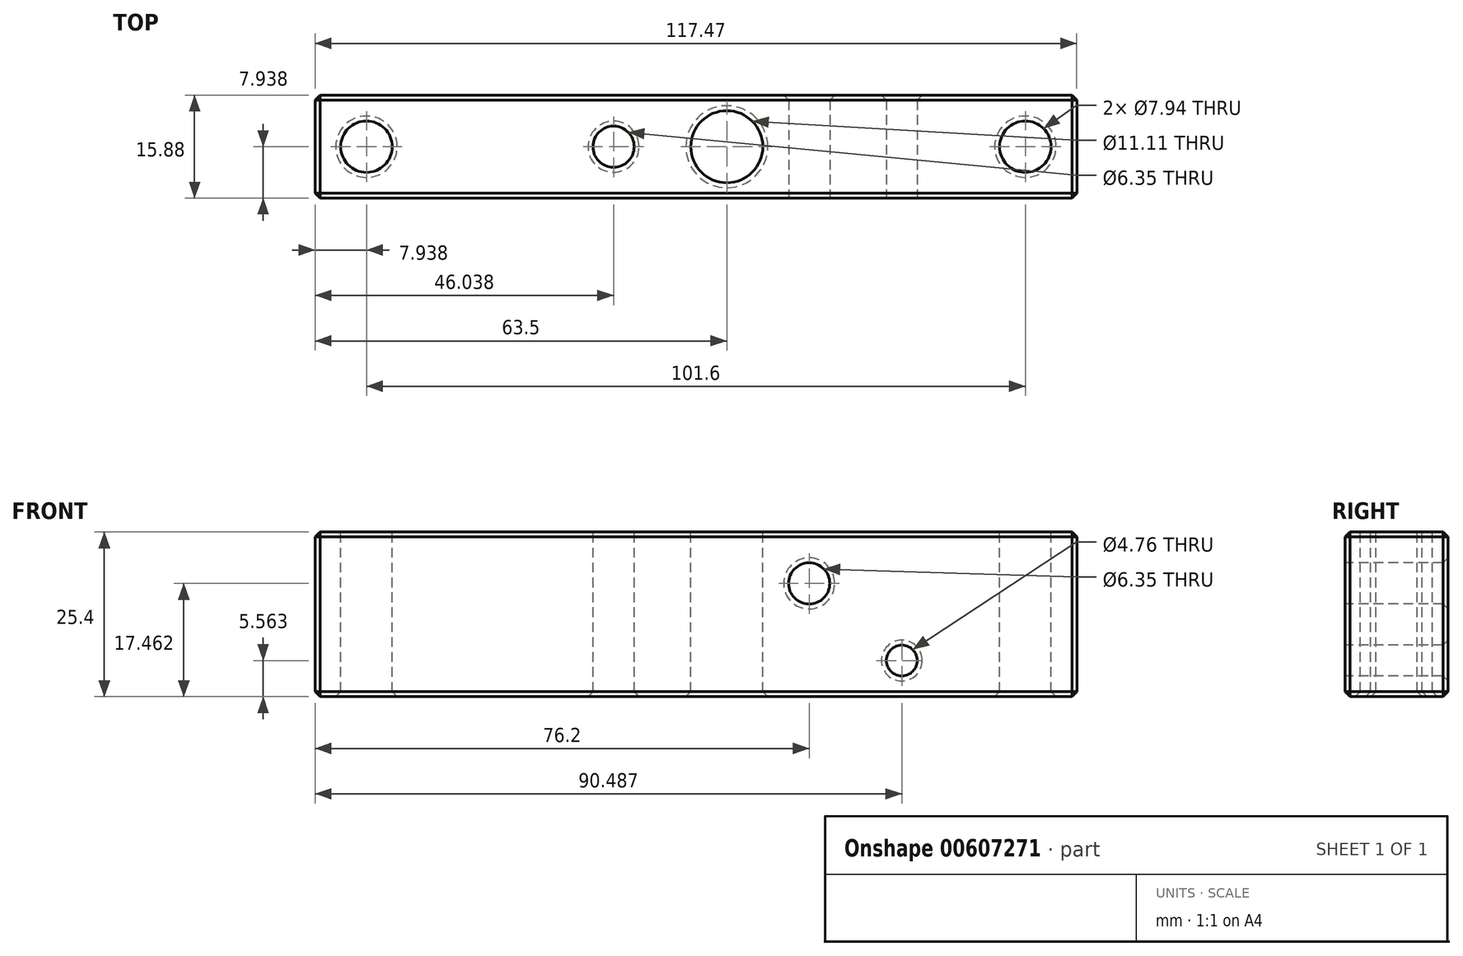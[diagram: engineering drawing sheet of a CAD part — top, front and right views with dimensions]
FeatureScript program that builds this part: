
annotation { "Feature Type Name" : "Feature", "Feature Type Description" : "" }
export const myFeature = defineFeature(function(context is Context, id is Id, definition is map)
    precondition{}
    {
        {
            var Q0;
            Q0=qCreatedBy(makeId("Top.planeOp"),FACE);
            var sketch = newSketch(context, id + "F0", { "sketchPlane" : qUnion([Q0])});
            skLineSegment(sketch, "E0.bottom", {"start": v(0, 0) * mm, "end": v(117.48, 0) * mm});
            skLineSegment(sketch, "E0.top", {"start": v(0, 15.88) * mm, "end": v(117.48, 15.88) * mm});
            skLineSegment(sketch, "E0.left", {"start": v(0, 0) * mm, "end": v(0, 15.88) * mm});
            skLineSegment(sketch, "E0.right", {"start": v(117.48, 0) * mm, "end": v(117.48, 15.88) * mm});
            skSolve(sketch);
        }
        {
            var Q0;
            Q0 = qSketchRegion(id + "F0", true);
            extrude(context, id + "F1", {"entities" : qUnion([Q0]), "depth" : 25.4 * mm, "offsetDistance" : 25.4 * mm});
        }
        {
            var Q0;
            Q0=makeQuery(id+"F1.opExtrude","CAP_FACE",FACE,{"disambiguationData":[OSD([sQuery(id+"F0.wireOp",EDGE,"E0.bottom"),sQuery(id+"F0.wireOp",EDGE,"E0.top"),sQuery(id+"F0.wireOp",EDGE,"E0.left"),sQuery(id+"F0.wireOp",EDGE,"E0.right")])],"isStart":false});
            var sketch = newSketch(context, id + "F2", { "sketchPlane" : qUnion([Q0])});
            skPoint(sketch, "E1.endSnap0", {"position": v(117.48, 7.94) * mm});
            skCircle(sketch, "E2", {"center": v(109.54, 7.94) * mm, "radius": 3.97 * mm});
            skCircle(sketch, "E3", {"center": v(7.94, 7.94) * mm, "radius": 3.97 * mm});
            skLineSegment(sketch, "E4", {"start": v(117.48, 7.94) * mm, "end": v(109.54, 7.94) * mm, "construction": true});
            skLineSegment(sketch, "E5", {"start": v(0, 7.94) * mm, "end": v(7.94, 7.94) * mm, "construction": true});
            skLineSegment(sketch, "E6", {"start": v(117.48, 7.94) * mm, "end": v(63.5, 7.94) * mm, "construction": true});
            skLineSegment(sketch, "E7", {"start": v(117.48, 7.94) * mm, "end": v(46.04, 7.94) * mm, "construction": true});
            skCircle(sketch, "E8", {"center": v(63.5, 7.94) * mm, "radius": 5.56 * mm});
            skCircle(sketch, "E9", {"center": v(46.04, 7.94) * mm, "radius": 3.18 * mm});
            skSolve(sketch);
        }
        {
            var Q0;
            Q0=makeQuery(id+"F2.imprint","IMPRINT",FACE,{"disambiguationData":[TD([[makeQuery(id+"F2.imprint","IMPRINT",EDGE,{"derivedFrom":sQuery(id+"F2.wireOp",EDGE,"E3")}),1.0]])]});
            var Q1;
            Q1=makeQuery(id+"F2.imprint","IMPRINT",FACE,{"disambiguationData":[TD([[makeQuery(id+"F2.imprint","IMPRINT",EDGE,{"derivedFrom":sQuery(id+"F2.wireOp",EDGE,"E9")}),1.0]])]});
            var Q2;
            Q2=makeQuery(id+"F2.imprint","IMPRINT",FACE,{"disambiguationData":[TD([[makeQuery(id+"F2.imprint","IMPRINT",EDGE,{"derivedFrom":sQuery(id+"F2.wireOp",EDGE,"E8")}),1.0]])]});
            var Q3;
            Q3=makeQuery(id+"F2.imprint","IMPRINT",FACE,{"disambiguationData":[TD([[makeQuery(id+"F2.imprint","IMPRINT",EDGE,{"derivedFrom":sQuery(id+"F2.wireOp",EDGE,"E2")}),1.0]])]});
            extrude(context, id + "F3", {"entities" : qUnion([Q0, Q1, Q2, Q3]), "operationType" : NewBodyOperationType.REMOVE, "endBound" : BoundingType.THROUGH_ALL, "oppositeDirection" : true, "depth" : 25.4 * mm, "offsetDistance" : 25.4 * mm});
        }
        {
            var Q0;
            Q0=makeQuery(id+"F1.opExtrude","SWEPT_FACE",FACE,{"disambiguationData":[OSD([sQuery(id+"F0.wireOp",EDGE,"E0.bottom")])]});
            var sketch = newSketch(context, id + "F4", { "sketchPlane" : qUnion([Q0])});
            skLineSegment(sketch, "E10", {"start": v(117.48, 0) * mm, "end": v(117.48, 5.56) * mm, "construction": true});
            skLineSegment(sketch, "E11", {"start": v(117.48, 5.56) * mm, "end": v(90.49, 5.56) * mm, "construction": true});
            skLineSegment(sketch, "E12", {"start": v(117.48, 0) * mm, "end": v(117.48, 17.46) * mm, "construction": true});
            skLineSegment(sketch, "E13", {"start": v(117.48, 17.46) * mm, "end": v(76.2, 17.46) * mm, "construction": true});
            skCircle(sketch, "E14", {"center": v(76.2, 17.46) * mm, "radius": 3.18 * mm});
            skCircle(sketch, "E15", {"center": v(90.49, 5.56) * mm, "radius": 2.38 * mm});
            skSolve(sketch);
        }
        {
            var Q0;
            Q0 = qSketchRegion(id + "F4", true);
            extrude(context, id + "F5", {"entities" : qUnion([Q0]), "operationType" : NewBodyOperationType.REMOVE, "endBound" : BoundingType.THROUGH_ALL, "oppositeDirection" : true, "depth" : 25.4 * mm, "offsetDistance" : 25.4 * mm});
        }
        {
            var Q0;
            Q0=makeQuery(id+"F5.boolean.opBoolean","COPY",EDGE,{"derivedFrom":makeQuery(id+"F5.opExtrude","CAP_EDGE",EDGE,{"disambiguationData":[OSD([sQuery(id+"F4.wireOp",EDGE,"E14")])],"isStart":true})});
            var Q1;
            Q1=makeQuery(id+"F5.boolean.opBoolean","COPY",EDGE,{"derivedFrom":makeQuery(id+"F5.opExtrude","CAP_EDGE",EDGE,{"disambiguationData":[OSD([sQuery(id+"F4.wireOp",EDGE,"E15")])],"isStart":true})});
            var Q2;
            Q2=makeQuery(id+"F3.boolean.opBoolean","COPY",EDGE,{"derivedFrom":makeQuery(id+"F3.opExtrude","CAP_EDGE",EDGE,{"disambiguationData":[OSD([sQuery(id+"F2.wireOp",EDGE,"E8")])],"isStart":true})});
            var Q3;
            Q3=makeQuery(id+"F3.boolean.opBoolean","COPY",EDGE,{"derivedFrom":makeQuery(id+"F3.opExtrude","CAP_EDGE",EDGE,{"disambiguationData":[OSD([sQuery(id+"F2.wireOp",EDGE,"E9")])],"isStart":true})});
            var Q4;
            Q4=makeQuery(id+"F3.boolean.opBoolean","COPY",EDGE,{"derivedFrom":makeQuery(id+"F3.opExtrude","CAP_EDGE",EDGE,{"disambiguationData":[OSD([sQuery(id+"F2.wireOp",EDGE,"E2")])],"isStart":true})});
            var Q5;
            Q5=makeQuery(id+"F1.opExtrude","CAP_EDGE",EDGE,{"disambiguationData":[OSD([sQuery(id+"F0.wireOp",EDGE,"E0.bottom")])],"isStart":false});
            var Q6;
            Q6=makeQuery(id+"F1.opExtrude","CAP_EDGE",EDGE,{"disambiguationData":[OSD([sQuery(id+"F0.wireOp",EDGE,"E0.bottom")])],"isStart":true});
            var Q7;
            Q7=makeQuery(id+"F1.opExtrude","SWEPT_EDGE",EDGE,{"disambiguationData":[OSD([sQuery(id+"F0.wireOp",EDGE,"E0.bottom"),sQuery(id+"F0.wireOp",EDGE,"E0.right")])]});
            var Q8;
            Q8=makeQuery(id+"F1.opExtrude","SWEPT_EDGE",EDGE,{"disambiguationData":[OSD([sQuery(id+"F0.wireOp",EDGE,"E0.bottom"),sQuery(id+"F0.wireOp",EDGE,"E0.left")])]});
            var Q9;
            Q9=makeQuery(id+"F1.opExtrude","CAP_EDGE",EDGE,{"disambiguationData":[OSD([sQuery(id+"F0.wireOp",EDGE,"E0.left")])],"isStart":false});
            var Q10;
            Q10=makeQuery(id+"F1.opExtrude","SWEPT_EDGE",EDGE,{"disambiguationData":[OSD([sQuery(id+"F0.wireOp",EDGE,"E0.top"),sQuery(id+"F0.wireOp",EDGE,"E0.left")])]});
            var Q11;
            Q11=makeQuery(id+"F1.opExtrude","CAP_EDGE",EDGE,{"disambiguationData":[OSD([sQuery(id+"F0.wireOp",EDGE,"E0.left")])],"isStart":true});
            var Q12;
            Q12=makeQuery(id+"F1.opExtrude","CAP_EDGE",EDGE,{"disambiguationData":[OSD([sQuery(id+"F0.wireOp",EDGE,"E0.top")])],"isStart":true});
            var Q13;
            Q13=makeQuery(id+"F3.boolean.opBoolean","INTERSECT",EDGE,{"derivedFrom":[makeQuery(id+"F1.opExtrude","CAP_FACE",FACE,{"disambiguationData":[OSD([sQuery(id+"F0.wireOp",EDGE,"E0.bottom"),sQuery(id+"F0.wireOp",EDGE,"E0.top"),sQuery(id+"F0.wireOp",EDGE,"E0.left"),sQuery(id+"F0.wireOp",EDGE,"E0.right")])],"isStart":true}),makeQuery(id+"F3.opExtrude","SWEPT_FACE",FACE,{"disambiguationData":[OSD([sQuery(id+"F2.wireOp",EDGE,"E3")])]})]});
            var Q14;
            Q14=makeQuery(id+"F3.boolean.opBoolean","INTERSECT",EDGE,{"derivedFrom":[makeQuery(id+"F1.opExtrude","CAP_FACE",FACE,{"disambiguationData":[OSD([sQuery(id+"F0.wireOp",EDGE,"E0.bottom"),sQuery(id+"F0.wireOp",EDGE,"E0.top"),sQuery(id+"F0.wireOp",EDGE,"E0.left"),sQuery(id+"F0.wireOp",EDGE,"E0.right")])],"isStart":true}),makeQuery(id+"F3.opExtrude","SWEPT_FACE",FACE,{"disambiguationData":[OSD([sQuery(id+"F2.wireOp",EDGE,"E9")])]})]});
            var Q15;
            Q15=makeQuery(id+"F3.boolean.opBoolean","INTERSECT",EDGE,{"derivedFrom":[makeQuery(id+"F1.opExtrude","CAP_FACE",FACE,{"disambiguationData":[OSD([sQuery(id+"F0.wireOp",EDGE,"E0.bottom"),sQuery(id+"F0.wireOp",EDGE,"E0.top"),sQuery(id+"F0.wireOp",EDGE,"E0.left"),sQuery(id+"F0.wireOp",EDGE,"E0.right")])],"isStart":true}),makeQuery(id+"F3.opExtrude","SWEPT_FACE",FACE,{"disambiguationData":[OSD([sQuery(id+"F2.wireOp",EDGE,"E8")])]})]});
            var Q16;
            Q16=makeQuery(id+"F1.opExtrude","CAP_EDGE",EDGE,{"disambiguationData":[OSD([sQuery(id+"F0.wireOp",EDGE,"E0.top")])],"isStart":false});
            var Q17;
            Q17=makeQuery(id+"F5.boolean.opBoolean","INTERSECT",EDGE,{"derivedFrom":[makeQuery(id+"F1.opExtrude","SWEPT_FACE",FACE,{"disambiguationData":[OSD([sQuery(id+"F0.wireOp",EDGE,"E0.top")])]}),makeQuery(id+"F5.opExtrude","SWEPT_FACE",FACE,{"disambiguationData":[OSD([sQuery(id+"F4.wireOp",EDGE,"E14")])]})]});
            var Q18;
            Q18=makeQuery(id+"F5.boolean.opBoolean","INTERSECT",EDGE,{"derivedFrom":[makeQuery(id+"F1.opExtrude","SWEPT_FACE",FACE,{"disambiguationData":[OSD([sQuery(id+"F0.wireOp",EDGE,"E0.top")])]}),makeQuery(id+"F5.opExtrude","SWEPT_FACE",FACE,{"disambiguationData":[OSD([sQuery(id+"F4.wireOp",EDGE,"E15")])]})]});
            var Q19;
            Q19=makeQuery(id+"F3.boolean.opBoolean","COPY",EDGE,{"derivedFrom":makeQuery(id+"F3.opExtrude","CAP_EDGE",EDGE,{"disambiguationData":[OSD([sQuery(id+"F2.wireOp",EDGE,"E3")])],"isStart":true})});
            var Q20;
            Q20=makeQuery(id+"F1.opExtrude","CAP_EDGE",EDGE,{"disambiguationData":[OSD([sQuery(id+"F0.wireOp",EDGE,"E0.right")])],"isStart":false});
            var Q21;
            Q21=makeQuery(id+"F1.opExtrude","SWEPT_EDGE",EDGE,{"disambiguationData":[OSD([sQuery(id+"F0.wireOp",EDGE,"E0.top"),sQuery(id+"F0.wireOp",EDGE,"E0.right")])]});
            var Q22;
            Q22=makeQuery(id+"F1.opExtrude","CAP_EDGE",EDGE,{"disambiguationData":[OSD([sQuery(id+"F0.wireOp",EDGE,"E0.right")])],"isStart":true});
            var Q23;
            Q23=makeQuery(id+"F3.boolean.opBoolean","INTERSECT",EDGE,{"derivedFrom":[makeQuery(id+"F1.opExtrude","CAP_FACE",FACE,{"disambiguationData":[OSD([sQuery(id+"F0.wireOp",EDGE,"E0.bottom"),sQuery(id+"F0.wireOp",EDGE,"E0.top"),sQuery(id+"F0.wireOp",EDGE,"E0.left"),sQuery(id+"F0.wireOp",EDGE,"E0.right")])],"isStart":true}),makeQuery(id+"F3.opExtrude","SWEPT_FACE",FACE,{"disambiguationData":[OSD([sQuery(id+"F2.wireOp",EDGE,"E2")])]})]});
            chamfer(context, id + "F6", {"entities" : qUnion([Q0, Q1, Q2, Q3, Q4, Q5, Q6, Q7, Q8, Q9, Q10, Q11, Q12, Q13, Q14, Q15, Q16, Q17, Q18, Q19, Q20, Q21, Q22, Q23]), "width" : 0.76 * mm, "tangentPropagation" : true});
        }
    });
